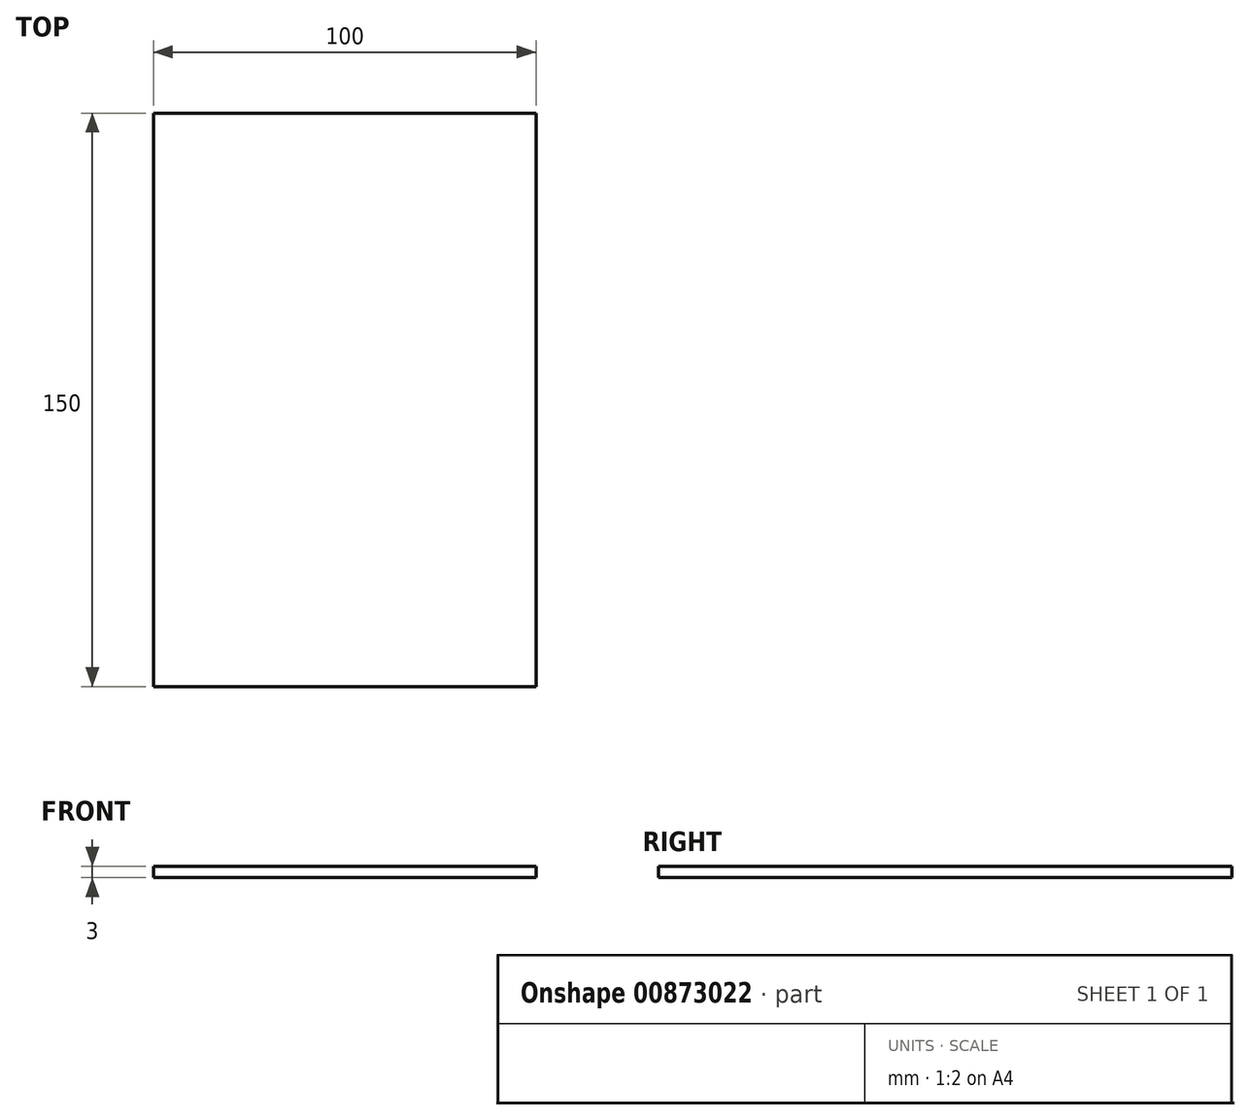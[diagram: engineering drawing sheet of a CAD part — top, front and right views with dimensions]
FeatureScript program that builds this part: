
annotation { "Feature Type Name" : "Feature", "Feature Type Description" : "" }
export const myFeature = defineFeature(function(context is Context, id is Id, definition is map)
    precondition{}
    {
        {
            var Q0;
            Q0=qCreatedBy(makeId("Top.planeOp"),FACE);
            var sketch = newSketch(context, id + "F0", { "sketchPlane" : qUnion([Q0])});
            skLineSegment(sketch, "E0.bottom", {"start": v(-50, -75) * mm, "end": v(50, -75) * mm});
            skLineSegment(sketch, "E0.top", {"start": v(-50, 75) * mm, "end": v(50, 75) * mm});
            skLineSegment(sketch, "E0.left", {"start": v(-50, -75) * mm, "end": v(-50, 75) * mm});
            skLineSegment(sketch, "E0.right", {"start": v(50, -75) * mm, "end": v(50, 75) * mm});
            skPoint(sketch, "E0.middle", {"position": v(0, 0) * mm});
            skSolve(sketch);
        }
        {
            var Q0;
            Q0 = qSketchRegion(id + "F0", true);
            extrude(context, id + "F1", {"entities" : qUnion([Q0]), "depth" : 3 * mm, "offsetDistance" : 25 * mm});
        }
    });
